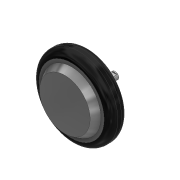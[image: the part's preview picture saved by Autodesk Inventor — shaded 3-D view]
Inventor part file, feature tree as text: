
AUTODESK INVENTOR PART (.ipt)
format: ipt  version: 2018 (Build 220112000, 112)  size: 184,832 bytes
history: native  units: mm
features: sketch x3, imported_body x1, extrude x1, revolve x1
ambient origin geometry x8: Origin, YZ Plane, XZ Plane, XY Plane, X Axis, Y Axis, Z Axis, Center Point
bodies: Solid1 (feature_tree)
feature tree (6):
  imported_body  "Base"
  extrude  "Cut"  Depth=110.0mm
  revolve  "Revolution2"  [1 undecoded]
  sketch  "Sketch1"  dims[d1=139.0mm d2=110.0mm]
  sketch  "Sketch2"  dims[d3=128.0mm d4=52.5mm]
  sketch  "Sketch3"  dims[d6=14.5mm d7=20.0mm d8=135.0deg d9=5.0mm d10=15.9mm d11=57.0mm d12=90.0deg d13=13.4mm d14=5.5mm d15=2.5mm d16=44.0mm d17=10.0mm d18=0.0mm d21=172.0mm d22=15.0mm d23=90.0deg]
note: 1 required parameter value undecoded (feature->parameter linkage not recoverable at this tier; creation-order binding heuristic only, values carry confidence <= 0.55)
